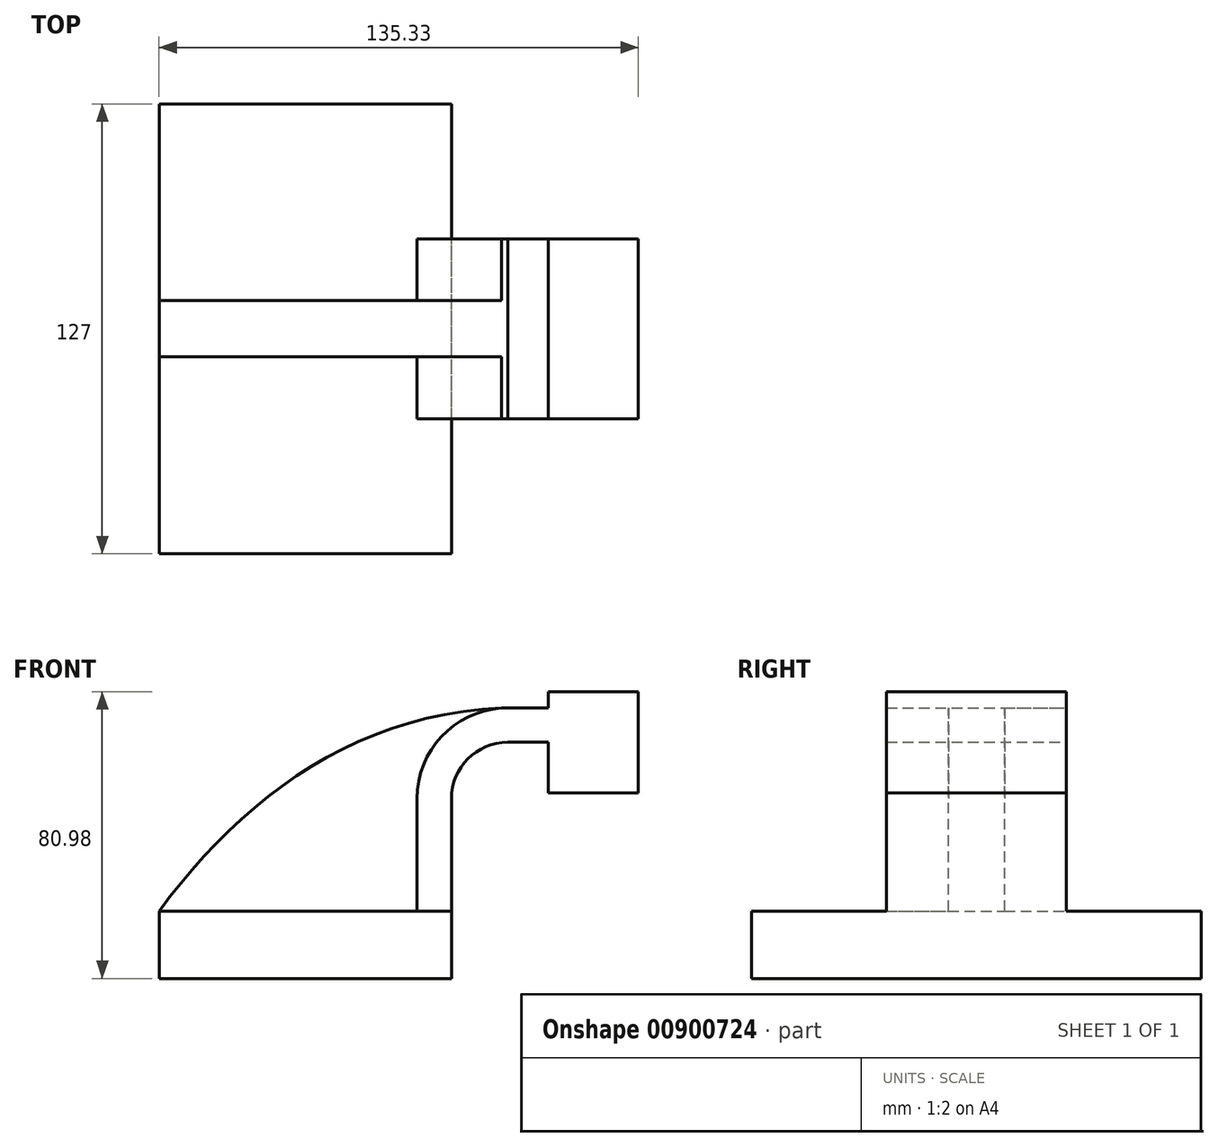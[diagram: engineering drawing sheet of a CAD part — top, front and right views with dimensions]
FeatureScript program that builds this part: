
annotation { "Feature Type Name" : "Feature", "Feature Type Description" : "" }
export const myFeature = defineFeature(function(context is Context, id is Id, definition is map)
    precondition{}
    {
        {
            var Q0;
            Q0=qCreatedBy(makeId("Front.planeOp"),FACE);
            var sketch = newSketch(context, id + "F0", { "sketchPlane" : qUnion([Q0])});
            skLineSegment(sketch, "E0.bottom", {"start": v(-41.28, -9.53) * mm, "end": v(41.28, -9.53) * mm});
            skLineSegment(sketch, "E0.top", {"start": v(-41.28, 9.53) * mm, "end": v(41.28, 9.53) * mm});
            skLineSegment(sketch, "E0.left", {"start": v(-41.28, -9.53) * mm, "end": v(-41.28, 9.53) * mm});
            skLineSegment(sketch, "E0.right", {"start": v(41.28, -9.53) * mm, "end": v(41.28, 9.53) * mm});
            skPoint(sketch, "E0.middle", {"position": v(0, 0) * mm});
            skLineSegment(sketch, "E1.bottom", {"start": v(68.65, 42.88) * mm, "end": v(119.45, 42.88) * mm});
            skLineSegment(sketch, "E1.top", {"start": v(68.65, 71.45) * mm, "end": v(119.45, 71.45) * mm});
            skLineSegment(sketch, "E1.left", {"start": v(68.65, 42.88) * mm, "end": v(68.65, 71.45) * mm});
            skLineSegment(sketch, "E1.right", {"start": v(119.45, 42.88) * mm, "end": v(119.45, 71.45) * mm});
            skPoint(sketch, "E1.middle", {"position": v(94.05, 57.16) * mm});
            skLineSegment(sketch, "E2", {"start": v(41.27, 9.53) * mm, "end": v(41.27, 41.29) * mm});
            skArc(sketch, "E3", {"start": v(41.27, 41.29) * mm, "mid": v(45.92, 52.51) * mm, "end": v(57.15, 57.16) * mm});
            skPoint(sketch, "E3.endSnap0", {"position": v(68.65, 57.16) * mm});
            skLineSegment(sketch, "E4", {"start": v(57.15, 57.16) * mm, "end": v(84.83, 57.16) * mm});
            skLineSegment(sketch, "E5.0", {"start": v(57.15, 66.87) * mm, "end": v(84.83, 66.87) * mm});
            skArc(sketch, "E5.1", {"start": v(31.57, 41.29) * mm, "mid": v(39.06, 59.38) * mm, "end": v(57.15, 66.87) * mm});
            skLineSegment(sketch, "E5.2", {"start": v(31.57, 9.53) * mm, "end": v(31.57, 41.29) * mm});
            skLineSegment(sketch, "E6", {"start": v(85.45, 42.88) * mm, "end": v(84.83, 71.45) * mm});
            skFitSpline(sketch, "E7", {"points": [v(-41.28, 9.52) * mm, v(57.15, 66.87) * mm], "startDerivative": vector(68.82, 93.3) * mm, "endDerivative": vector(130.02, 3.43) * mm});
            skLineSegment(sketch, "E8", {"start": v(94.05, 42.88) * mm, "end": v(94.05, 57.16) * mm});
            skLineSegment(sketch, "E9", {"start": v(94.05, 71.45) * mm, "end": v(94.05, 57.16) * mm});
            skSolve(sketch);
        }
        {
            var Q0;
            Q0=makeQuery(id+"F0.imprint","IMPRINT",FACE,{"disambiguationData":[TD([[makeQuery(id+"F0.imprint","IMPRINT",EDGE,{"derivedFrom":sQuery(id+"F0.wireOp",EDGE,"E0.bottom")}),1.0]])]});
            extrude(context, id + "F1", {"entities" : qUnion([Q0]), "endBound" : BoundingType.SYMMETRIC, "depth" : 127 * mm, "offsetDistance" : 25.4 * mm});
        }
        {
            var Q0;
            {var subQ1=sQuery(id+"F0.wireOp",EDGE,"E2");Q0=makeQuery(id+"F0.imprint","IMPRINT",FACE,{"disambiguationData":[TD([[makeQuery(id+"F0.imprint","IMPRINT",EDGE,{"derivedFrom":subQ1}),1.0]])]});}
            extrude(context, id + "F2", {"entities" : qUnion([Q0]), "operationType" : NewBodyOperationType.ADD, "endBound" : BoundingType.SYMMETRIC, "depth" : 50.8 * mm, "offsetDistance" : 25.4 * mm});
        }
        {
            var Q0;
            {var subQ3=sQuery(id+"F0.wireOp",EDGE,"E5.2");Q0=makeQuery(id+"F0.imprint","IMPRINT",FACE,{"disambiguationData":[TD([[makeQuery(id+"F0.imprint","IMPRINT",EDGE,{"derivedFrom":subQ3}),1.0]])]});}
            extrude(context, id + "F3", {"entities" : qUnion([Q0]), "operationType" : NewBodyOperationType.ADD, "endBound" : BoundingType.SYMMETRIC, "depth" : 15.88 * mm, "offsetDistance" : 25.4 * mm});
        }
        {
            var Q0;
            {var subQ5=sQuery(id+"F0.wireOp",EDGE,"E6");Q0=makeQuery(id+"F0.imprint","IMPRINT",FACE,{"disambiguationData":[TD([[makeQuery(id+"F0.imprint","IMPRINT",EDGE,{"derivedFrom":subQ5}),1.0]])]});}
            var Q1;
            {var subQ1=sQuery(id+"F0.wireOp",EDGE,"E6");Q1=makeQuery(id+"F0.imprint","IMPRINT",FACE,{"disambiguationData":[TD([[makeQuery(id+"F0.imprint","IMPRINT",EDGE,{"derivedFrom":subQ1}),-1.0]])]});}
            extrude(context, id + "F4", {"entities" : qUnion([Q0, Q1]), "operationType" : NewBodyOperationType.ADD, "endBound" : BoundingType.SYMMETRIC, "depth" : 50.8 * mm, "offsetDistance" : 25.4 * mm});
        }
    });
